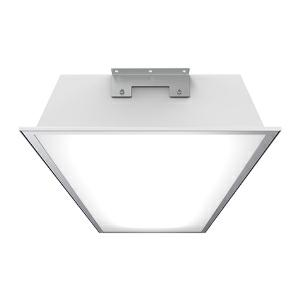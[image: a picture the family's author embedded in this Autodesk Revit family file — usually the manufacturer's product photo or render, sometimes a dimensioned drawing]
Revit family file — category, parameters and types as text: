
# Revit family: 3f_filippi_-_beta_500_va_3f_filippi_-_52050_-_beta_500_200w-840_va_l870
name_source: partatom
category: Lighting Fixtures
units: mm (PartAtom-declared; Revit-internal decimal feet)

## family parameters
Cut with Voids When Loaded = No
Host = Face
Light Source = No
Part Type = Normal
Room Calculation Point = No
Round Connector Dimension = Use Diameter
Shared = No

## types (1)
- 3F Filippi - Beta 500 VA (1 x LED, 32079 lm, 198 W, 4000 K)
    Apparent Load = 198 VA
    Approval mark = CE
    CIE Flux Codes = 51 82 97 100 100
    Color Rendering = 80
    Color Temperature = 4000 K
    Control Gear = Electronic ballast
    Default Elevation = 1800 mm
    Description = ILLUMINOTECHNICAL
Luminous efficiency 100% (DLOR 100%, ULOR 0%).
Initial luminous flux of the luminaire 32079 lm.
Direct symmetric medium distribution.
Installation Interdistance Transv.D = 1.23 x hu - Long.D = 1.21 x hu.
Tabular UGR (CIE 117 - 4H-8H; S=0.25H; 70/50/20): RUG 26.6 - 27.1.
Beam angle: 102° - 104°.
Luminous efficacy 162 lm/W.
Lifetime (L93/B10): 30000 h. (tq+25°C)
Lifetime (L90/B10): 50000 h. (tq+25°C)
Lifetime (L85/B10): 80000 h. (tq+25°C)
Lifetime (L80/B10): 100000 h. (tq+25°C)
Lifetime (L85/B10): 50000 h. (tq+45°C)
Sudden decreased luminous flux after 50000 hours: 0% (C0).
Photobiological safety in compliance with IEC/TR 62778: RG0 risk exempt, (IEC 62471).
In compliance with IEC/EN 62722-2-1 - IEC/EN 62717 standards.

SOURCE
4 linear LED modules 50W/840.
Energy efficiency class (UE 2019/2020 - UE 2019/2015): C.
CIE 13.3 Colour rendering index: CRI >80 (R9 <50%).
IES TM-30 Fidelity Index: Rf = 84 Rg = 95.
CCT nominal colour temperature 4000 K.
Colour initial tolerance (MacAdam): SDCM 3.

MECHANICAL
Housing in white painted epoxy-polyester powder aluminium.
White aluminium non-iridescent high efficiency.
Frosted glass HST tempered, non-combustible.
Perimetrical frame in stainless steel with vandal-proof opening and stainless steel nuts and bolts.
Polyurethane foam seal, ecological, anti-aging, installed using a continuous automatic process with no joints.
Fixing bracket in stainless steel.
Luminaire with limited surface temperature. - D - (EN 60598-2-24)
Dimensions: 870x515 mm, height 105 mm. Weight 11.93 kg.
IP66 protection degree.
Mechanical strength to impacts IK08 (5 joule).
Glow-wire test resistance 960°C.

ELECTRICAL
Halogen Free electronic wiring 230V-50/60Hz, power factor 0.95, THD <25%, constant output current, class I, 2 driver.
Twin-circuit.
Power of the luminaire 198 W.
ENEC - CE.
SAFE FLICKER: PstLM=<1 and SVM=<0.4 (IEC TR 61547-1 and IEC TR 63158), to ensure a more comfortable and safe light.
Luminaire compliant with EN 60598-2-22 for power supply from a centralised emergency system CPSS (Central Power Supply System), not incorporated in the luminaire - high risk areas excluded. The default power and flux are 100% in AC and 100% in DC.
Ambient temperature from -20°C to +45°C.
Temperature class T6 max 85°C.
Quick connection via M20 3P connector with 9-13 mm tightening range.
Quick connection in polycarbonate with M20x1,5 cable gland, to access the terminal block positioned on a removable runner.
Relative humidity UR: <85%.

INSTALLATION
Ceiling / Suspended.
All accessories dedicated to this product are available on the Catalog and on our website www.3F-Filippi.com.

APPLICATIONS
Commercial and industrial environments and warehouses.

WARNING
Fixture not suitable for cold stores with an ambient temperature <0°C and/or relative humidity >85%.
Luminaire designed for disposal/recycling at end-of-life.
Replaceable (LED only) light source by a professional. Replaceable control gear by a professional.
    Height = 105 mm
    Lamp = 1 x LED
    Lamp Light Flux = 32079 lm
    Lamp Power = 198 W
    Lamp count = 1
    Length = 870 mm
    Lifetime = 50000 h
    Luminous efficacy = 162 lm/W
    Manufacturer = 3F Filippi
    ModVariant = No
    Model = 3F Filippi - 52050 - Beta 500 200W-840 VA L870
    Mounting Place = Ceiling
    Mounting Type = Pendant
    Number of Poles = 1
    OnlyDefault = Yes
    Power Factor = 1
    Product Name = 3F Filippi - Beta 500 VA
    Product group = pendant luminaire
    ProductGroupID = 9
    Protection Class = Protection class I
    Protection Degree = IP 66
    RLX_Detail_Level = 1
    RLX_Emergency_Light_Flux = 0 lm
    RLX_Emergency_Type = 0
    RLX_Emergency_Type_DB = No
    RlxData = <blob elided: 119369 chars, md5=8a6dd85f>
    Socket = socket
    Standby Power = 0 W
    System Light Flux = 32080 lm
    System Power = 198 W
    Type Comments = Product without accessories
    Type Image = 3ffilippi_beta_500_va.jpg
    URL = http://relux.com
    VarID = ---
    Voltage = 0 V
    Weight = 0.00 kg
    Width = 515 mm

## geometry (parser evidence)
native form markers: Blend x4, Sweep x11
no freeform markers — native parametric forms only
